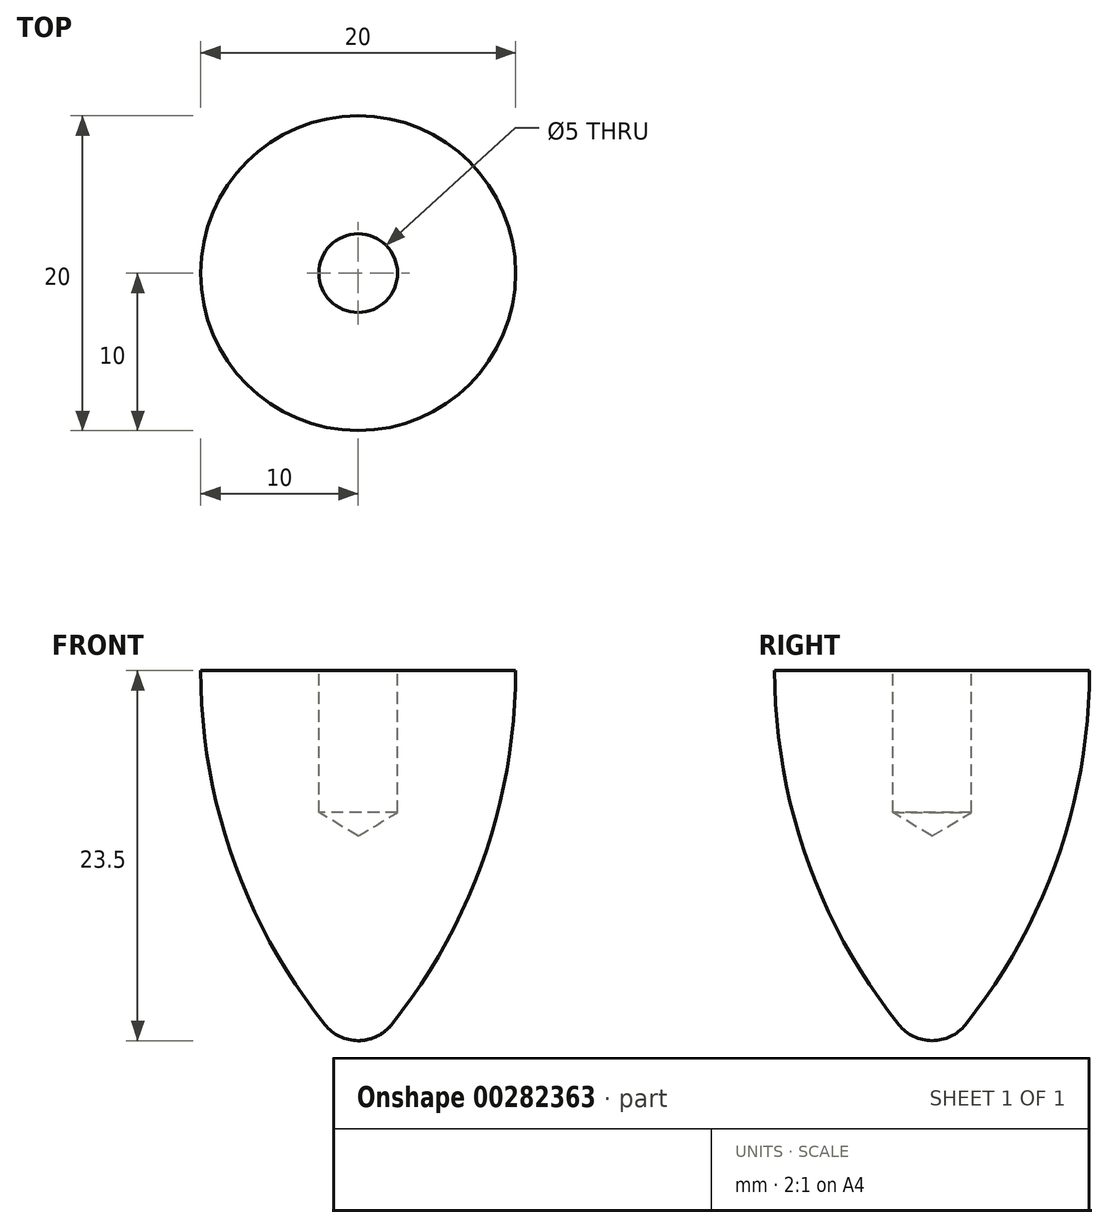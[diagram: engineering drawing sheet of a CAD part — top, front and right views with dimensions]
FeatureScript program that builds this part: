
annotation { "Feature Type Name" : "Feature", "Feature Type Description" : "" }
export const myFeature = defineFeature(function(context is Context, id is Id, definition is map)
    precondition{}
    {
        {
            var Q0;
            Q0=qCreatedBy(makeId("Front.planeOp"),FACE);
            var sketch = newSketch(context, id + "F0", { "sketchPlane" : qUnion([Q0])});
            skLineSegment(sketch, "E0", {"start": v(0, 0) * mm, "end": v(0, -23.5) * mm});
            skLineSegment(sketch, "E1", {"start": v(0, 0) * mm, "end": v(10, 0) * mm});
            skLineSegment(sketch, "E2", {"start": v(10, 0) * mm, "end": v(10, 5.54) * mm, "construction": true});
            skArc(sketch, "E3", {"start": v(0, -23.5) * mm, "mid": v(1.17, -23.23) * mm, "end": v(2.12, -22.48) * mm});
            skArc(sketch, "E4", {"start": v(2.12, -22.48) * mm, "mid": v(7.97, -11.91) * mm, "end": v(10, 0) * mm});
            skLineSegment(sketch, "E5", {"start": v(0, -23.5) * mm, "end": v(-2.48, -23.5) * mm, "construction": true});
            skSolve(sketch);
        }
        {
            var Q0;
            Q0=qSketchRegion(id+"F0",true);
            var Q1;
            Q1=sQuery(id+"F0.wireOp",EDGE,"E0");
            revolve(context, id + "F1", {"entities" : qUnion([Q0]), "axis" : qUnion([Q1]), "revolveType" : RevolveType.FULL});
        }
        {
            var Q0;
            Q0=makeQuery(id+"F1.opRevolve","SWEPT_FACE",FACE,{"disambiguationData":[OSD([sQuery(id+"F0.wireOp",EDGE,"E1")])]});
            var sketch = newSketch(context, id + "F2", { "sketchPlane" : qUnion([Q0])});
            skPoint(sketch, "E6", {"position": v(0, 0) * mm});
            skSolve(sketch);
        }
        {
            var Q0;
            Q0=sQuery(id+"F2.wireOp",VERTEX,"E6");
            var Q1;
            Q1=makeQuery(id+"F1.opRevolve","SWEPT_BODY",BODY,{"disambiguationData":[OSD([sQuery(id+"F0.wireOp",EDGE,"E0"),sQuery(id+"F0.wireOp",EDGE,"E1"),sQuery(id+"F0.wireOp",EDGE,"E3"),sQuery(id+"F0.wireOp",EDGE,"E4")])]});
            hole(context, id + "F3", {"style" : HoleStyle.SIMPLE, "endStyle" : HoleEndStyle.BLIND, "standardTappedOrClearance" : lookupTablePath({ "standard" : "ISO", "engagement" : "75%", "pitch" : "1 mm", "size" : "M6", "type" : "Tapped" }), "standardBlindInLast" : lookupTablePath({ "standard" : "ISO", "engagement" : "75%", "pitch" : "1 mm", "size" : "M6", "type" : "Tapped" }), "holeDiameter" : 5 * mm, "showTappedDepth" : true, "holeDepth" : 9 * mm, "tappedDepth" : 6 * mm, "tapClearance" : 3, "startFromSketch" : true, "locations" : qUnion([Q0]), "scope" : qUnion([Q1]), "majorDiameter" : 6 * mm});
        }
    });
